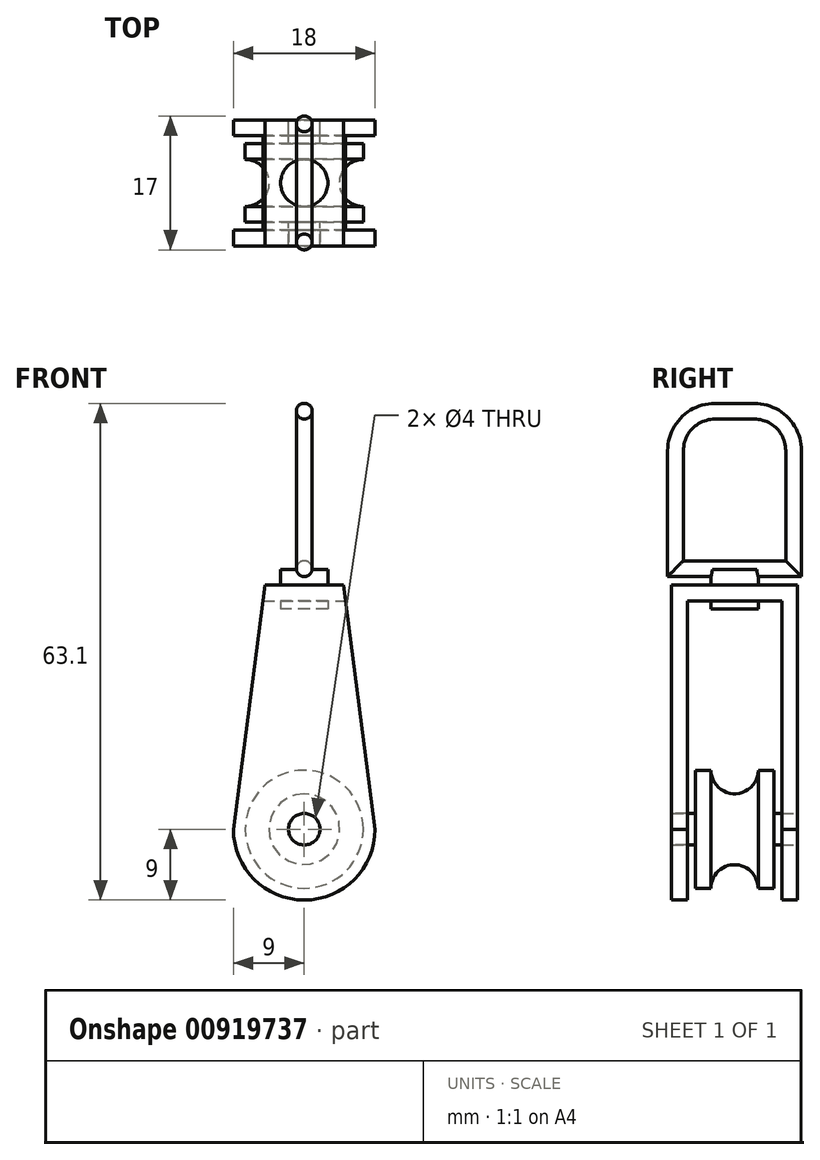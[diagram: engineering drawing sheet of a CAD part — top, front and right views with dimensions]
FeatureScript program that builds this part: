
annotation { "Feature Type Name" : "Feature", "Feature Type Description" : "" }
export const myFeature = defineFeature(function(context is Context, id is Id, definition is map)
    precondition{}
    {
        {
            var Q0;
            Q0=qCreatedBy(makeId("Right.planeOp"),FACE);
            var sketch = newSketch(context, id + "F0", { "sketchPlane" : qUnion([Q0])});
            skLineSegment(sketch, "E0", {"start": v(0, 0) * mm, "end": v(5, 0) * mm});
            skLineSegment(sketch, "E1", {"start": v(0, 0) * mm, "end": v(-5, 0) * mm});
            skLineSegment(sketch, "E2", {"start": v(0, 0) * mm, "end": v(0, 7.5) * mm, "construction": true});
            skPoint(sketch, "E3", {"position": v(0, 4.5) * mm});
            skLineSegment(sketch, "E4.0", {"start": v(3, 0) * mm, "end": v(3, 7.5) * mm, "construction": true});
            skLineSegment(sketch, "E5.0", {"start": v(-3, 0) * mm, "end": v(-3, 7.5) * mm, "construction": true});
            skArc(sketch, "E6", {"start": v(-3, 7.5) * mm, "mid": v(0, 4.5) * mm, "end": v(3, 7.5) * mm});
            skLineSegment(sketch, "E7", {"start": v(3, 7.5) * mm, "end": v(5, 7.5) * mm});
            skLineSegment(sketch, "E8", {"start": v(5, 7.5) * mm, "end": v(5, 0) * mm});
            skLineSegment(sketch, "E9", {"start": v(-3, 7.5) * mm, "end": v(-5, 7.5) * mm});
            skLineSegment(sketch, "E10", {"start": v(-5, 7.5) * mm, "end": v(-5, 0) * mm});
            skSolve(sketch);
        }
        {
            var Q0;
            Q0=makeQuery(id+"F0.imprint","IMPRINT",FACE,{"disambiguationData":[TD([[makeQuery(id+"F0.imprint","IMPRINT",EDGE,{"derivedFrom":sQuery(id+"F0.wireOp",EDGE,"E0")}),1.0]])]});
            var Q1;
            Q1=sQuery(id+"F0.wireOp",EDGE,"E1");
            revolve(context, id + "F1", {"surfaceOperationType" : NewSurfaceOperationType.NEW, "entities" : qUnion([Q0]), "axis" : qUnion([Q1]), "revolveType" : RevolveType.FULL});
        }
        {
            var Q0;
            Q0=makeQuery(id+"F1.opRevolve","SWEPT_FACE",FACE,{"disambiguationData":[OSD([sQuery(id+"F0.wireOp",EDGE,"E8")])]});
            var sketch = newSketch(context, id + "F2", { "sketchPlane" : qUnion([Q0])});
            skCircle(sketch, "E11", {"center": v(0, 0) * mm, "radius": 2 * mm});
            skSolve(sketch);
        }
        {
            var Q0;
            Q0=makeQuery(id+"F2.imprint","IMPRINT",FACE,{"disambiguationData":[TD([[makeQuery(id+"F2.imprint","IMPRINT",EDGE,{"derivedFrom":sQuery(id+"F2.wireOp",EDGE,"E11")}),1.0]])]});
            var Q1;
            Q1=makeQuery(id+"F1.opRevolve","SWEPT_FACE",FACE,{"disambiguationData":[OSD([sQuery(id+"F0.wireOp",EDGE,"E10")])]});
            extrude(context, id + "F3", {"entities" : qUnion([Q0]), "operationType" : NewBodyOperationType.ADD, "endBound" : BoundingType.UP_TO_SURFACE, "oppositeDirection" : true, "depth" : 25 * mm, "endBoundEntityFace" : qUnion([Q1]), "hasOffset" : true, "offsetDistance" : 3 * mm, "offsetOppositeDirection" : true, "hasSecondDirection" : true, "secondDirectionOppositeDirection" : false, "secondDirectionDepth" : 3 * mm});
        }
        {
            var Q0;
            Q0=makeQuery(id+"F3.opExtrude","CAP_FACE",FACE,{"disambiguationData":[OSD([sQuery(id+"F2.wireOp",EDGE,"E11")])],"isStart":true});
            var sketch = newSketch(context, id + "F4", { "sketchPlane" : qUnion([Q0])});
            skCircle(sketch, "E12.0", {"center": v(0, 0) * mm, "radius": 7.5 * mm});
            skCircle(sketch, "E13.0", {"center": v(0, 0) * mm, "radius": 2 * mm});
            skLineSegment(sketch, "E14", {"start": v(0, 0) * mm, "end": v(-7.5, 0) * mm, "construction": true});
            skLineSegment(sketch, "E15", {"start": v(0, 0) * mm, "end": v(7.5, 0) * mm, "construction": true});
            skLineSegment(sketch, "E16", {"start": v(7.5, 0) * mm, "end": v(9, 0) * mm, "construction": true});
            skLineSegment(sketch, "E17", {"start": v(-7.5, 0) * mm, "end": v(-9, 0) * mm, "construction": true});
            skLineSegment(sketch, "E18", {"start": v(0, 0) * mm, "end": v(0, -7.5) * mm, "construction": true});
            skLineSegment(sketch, "E19", {"start": v(0, -7.5) * mm, "end": v(0, -9) * mm, "construction": true});
            skArc(sketch, "E20", {"start": v(-9, 0) * mm, "mid": v(0, -9) * mm, "end": v(9, 0) * mm});
            skLineSegment(sketch, "E21", {"start": v(0, 0) * mm, "end": v(0, 49) * mm, "construction": true});
            skPoint(sketch, "E22", {"position": v(0, 33) * mm});
            skPoint(sketch, "E23", {"position": v(0, 31) * mm});
            skLineSegment(sketch, "E24", {"start": v(0, 31) * mm, "end": v(-5, 31) * mm});
            skLineSegment(sketch, "E25", {"start": v(0, 31) * mm, "end": v(5, 31) * mm});
            skLineSegment(sketch, "E26", {"start": v(5, 31) * mm, "end": v(9, 0) * mm});
            skLineSegment(sketch, "E27", {"start": v(-5, 31) * mm, "end": v(-9, 0) * mm});
            skSolve(sketch);
        }
        {
            var Q0;
            Q0=makeQuery(id+"F4.imprint","IMPRINT",FACE,{"disambiguationData":[TD([[makeQuery(id+"F4.imprint","IMPRINT",EDGE,{"derivedFrom":sQuery(id+"F4.wireOp",EDGE,"E12.0")}),-1.0]])]});
            var Q1;
            Q1=makeQuery(id+"F4.imprint","IMPRINT",FACE,{"disambiguationData":[TD([[makeQuery(id+"F4.imprint","IMPRINT",EDGE,{"derivedFrom":sQuery(id+"F4.wireOp",EDGE,"E12.0")}),1.0]])]});
            extrude(context, id + "F5", {"entities" : qUnion([Q0, Q1]), "oppositeDirection" : true, "depth" : 2 * mm, "offsetDistance" : 25 * mm});
        }
        {
            var Q0;
            Q0=makeQuery(id+"F5.opExtrude","SWEPT_BODY",BODY,{"disambiguationData":[OSD([sQuery(id+"F4.wireOp",EDGE,"E13.0"),sQuery(id+"F4.wireOp",EDGE,"E20"),sQuery(id+"F4.wireOp",EDGE,"E24"),sQuery(id+"F4.wireOp",EDGE,"E25"),sQuery(id+"F4.wireOp",EDGE,"E26"),sQuery(id+"F4.wireOp",EDGE,"E27")])]});
            var Q1;
            Q1=qCreatedBy(makeId("Front.planeOp"),FACE);
            mirror(context, id + "F6", {"entities" : qUnion([Q0]), "mirrorPlane" : qUnion([Q1])});
        }
        {
            var Q0;
            Q0=makeQuery(id+"F5.opExtrude","CAP_FACE",FACE,{"disambiguationData":[OSD([sQuery(id+"F4.wireOp",EDGE,"E13.0"),sQuery(id+"F4.wireOp",EDGE,"E20"),sQuery(id+"F4.wireOp",EDGE,"E24"),sQuery(id+"F4.wireOp",EDGE,"E25"),sQuery(id+"F4.wireOp",EDGE,"E26"),sQuery(id+"F4.wireOp",EDGE,"E27")])],"isStart":true});
            var sketch = newSketch(context, id + "F7", { "sketchPlane" : qUnion([Q0])});
            skLineSegment(sketch, "E28", {"start": v(0, 31) * mm, "end": v(0, 29) * mm, "construction": true});
            skLineSegment(sketch, "E29.0", {"start": v(-5, 31) * mm, "end": v(-9, 0) * mm});
            skLineSegment(sketch, "E30.0", {"start": v(5, 31) * mm, "end": v(9, 0) * mm});
            skLineSegment(sketch, "E31", {"start": v(0, 29) * mm, "end": v(-5.26, 29) * mm});
            skLineSegment(sketch, "E32", {"start": v(0, 29) * mm, "end": v(5.26, 29) * mm});
            skSolve(sketch);
        }
        {
            var Q0;
            {var subQ0=sQuery(id+"F7.wireOp",EDGE,"E31");Q0=makeQuery(id+"F7.imprint","IMPRINT",FACE,{"disambiguationData":[TD([[makeQuery(id+"F7.imprint","IMPRINT",EDGE,{"derivedFrom":subQ0}),-1.0]])]});}
            var Q1;
            Q1=makeQuery(id+"F6.opPattern","COPY",FACE,{"derivedFrom":makeQuery(id+"F5.opExtrude","CAP_FACE",FACE,{"disambiguationData":[OSD([sQuery(id+"F4.wireOp",EDGE,"E13.0"),sQuery(id+"F4.wireOp",EDGE,"E20"),sQuery(id+"F4.wireOp",EDGE,"E24"),sQuery(id+"F4.wireOp",EDGE,"E25"),sQuery(id+"F4.wireOp",EDGE,"E26"),sQuery(id+"F4.wireOp",EDGE,"E27")])],"isStart":false}),"instanceName":"1"});
            extrude(context, id + "F8", {"entities" : qUnion([Q0]), "operationType" : NewBodyOperationType.ADD, "endBound" : BoundingType.UP_TO_SURFACE, "oppositeDirection" : true, "depth" : 25 * mm, "endBoundEntityFace" : qUnion([Q1]), "offsetDistance" : 25 * mm});
        }
        {
            var Q0;
            {var subQ0=sQuery(id+"F4.wireOp",EDGE,"E25");var subQ1=sQuery(id+"F4.wireOp",EDGE,"E24");var subQ2=makeQuery(id+"F5.opExtrude","SWEPT_FACE",FACE,{"disambiguationData":[OSD([subQ1,subQ0])]});Q0=makeQuery(id+"F8.boolean.opBoolean","MERGE",FACE,{"derivedFrom":[subQ2,makeQuery(id+"F6.opPattern","COPY",FACE,{"derivedFrom":subQ2,"instanceName":"1"}),makeQuery(id+"F8.opExtrude","SWEPT_FACE",FACE,{"disambiguationData":[OSD([subQ1,subQ0])]})]});}
            var sketch = newSketch(context, id + "F9", { "sketchPlane" : qUnion([Q0])});
            skCircle(sketch, "E33", {"center": v(0, 0) * mm, "radius": 3 * mm});
            skSolve(sketch);
        }
        {
            var Q0;
            Q0=makeQuery(id+"F9.imprint","IMPRINT",FACE,{"disambiguationData":[TD([[makeQuery(id+"F9.imprint","IMPRINT",EDGE,{"derivedFrom":sQuery(id+"F9.wireOp",EDGE,"E33")}),1.0]])]});
            extrude(context, id + "F10", {"entities" : qUnion([Q0]), "operationType" : NewBodyOperationType.ADD, "depth" : 2 * mm, "offsetDistance" : 25 * mm, "hasSecondDirection" : true, "secondDirectionOppositeDirection" : true, "secondDirectionDepth" : 3 * mm});
        }
        {
            var Q0;
            Q0=qCreatedBy(makeId("Front.planeOp"),FACE);
            var sketch = newSketch(context, id + "F11", { "sketchPlane" : qUnion([Q0])});
            skLineSegment(sketch, "E34.0", {"start": v(-3, 33) * mm, "end": v(3, 33) * mm});
            skLineSegment(sketch, "E35", {"start": v(0, 33) * mm, "end": v(0, 33.1) * mm, "construction": true});
            skPoint(sketch, "E36", {"position": v(0, 33.1) * mm});
            skCircle(sketch, "E37", {"center": v(0, 33.1) * mm, "radius": 1 * mm});
            skSolve(sketch);
        }
        {
            var Q0;
            Q0=qCreatedBy(makeId("Right.planeOp"),FACE);
            var sketch = newSketch(context, id + "F12", { "sketchPlane" : qUnion([Q0])});
            skPoint(sketch, "E38.0", {"position": v(0, 33.1) * mm});
            skLineSegment(sketch, "E39", {"start": v(0, 33.1) * mm, "end": v(7.5, 33.1) * mm});
            skLineSegment(sketch, "E40", {"start": v(7.5, 33.1) * mm, "end": v(7.5, 48.1) * mm});
            skLineSegment(sketch, "E41", {"start": v(2.5, 53.1) * mm, "end": v(-2.5, 53.1) * mm});
            skLineSegment(sketch, "E42", {"start": v(-7.5, 48.1) * mm, "end": v(-7.5, 33.1) * mm});
            skLineSegment(sketch, "E43", {"start": v(-7.5, 33.1) * mm, "end": v(0, 33.1) * mm});
            skPoint(sketch, "E44.visualSharp", {"position": v(7.5, 53.1) * mm});
            skArc(sketch, "E44.filletArc", {"start": v(7.5, 48.1) * mm, "mid": v(6.04, 51.64) * mm, "end": v(2.5, 53.1) * mm});
            skPoint(sketch, "E45.visualSharp", {"position": v(-7.5, 53.1) * mm});
            skArc(sketch, "E45.filletArc", {"start": v(-2.5, 53.1) * mm, "mid": v(-6.04, 51.64) * mm, "end": v(-7.5, 48.1) * mm});
            skSolve(sketch);
        }
        {
            var Q0;
            Q0=makeQuery(id+"F11.imprint","IMPRINT",FACE,{"disambiguationData":[TD([[makeQuery(id+"F11.imprint","IMPRINT",EDGE,{"derivedFrom":sQuery(id+"F11.wireOp",EDGE,"E37")}),1.0]])]});
            var Q1;
            Q1=sQuery(id+"F12.wireOp",EDGE,"E39");
            var Q2;
            Q2=sQuery(id+"F12.wireOp",EDGE,"E40");
            var Q3;
            Q3=sQuery(id+"F12.wireOp",EDGE,"E44.filletArc");
            var Q4;
            Q4=sQuery(id+"F12.wireOp",EDGE,"E41");
            var Q5;
            Q5=sQuery(id+"F12.wireOp",EDGE,"E45.filletArc");
            var Q6;
            Q6=sQuery(id+"F12.wireOp",EDGE,"E42");
            var Q7;
            Q7=sQuery(id+"F12.wireOp",EDGE,"E43");
            sweep(context, id + "F13", {"operationType" : NewBodyOperationType.ADD, "profiles" : qUnion([Q0]), "path" : qUnion([Q1, Q2, Q3, Q4, Q5, Q6, Q7])});
        }
        {
            var Q0;
            Q0=qCreatedBy(makeId("Front.planeOp"),FACE);
            var sketch = newSketch(context, id + "F14", { "sketchPlane" : qUnion([Q0])});
            skLineSegment(sketch, "E46", {"start": v(0, 0) * mm, "end": v(0, 7.5) * mm, "construction": true});
            skLineSegment(sketch, "E47", {"start": v(3, 7.5) * mm, "end": v(5, 7.5) * mm});
            skLineSegment(sketch, "E48", {"start": v(-5, 7.5) * mm, "end": v(-3, 7.5) * mm});
            skLineSegment(sketch, "E49", {"start": v(-3, 7.5) * mm, "end": v(3, 7.5) * mm, "construction": true});
            skSolve(sketch);
        }
        {
            var Q0;
            Q0=qCreatedBy(makeId("Front.planeOp"),FACE);
            var sketch = newSketch(context, id + "F15", { "sketchPlane" : qUnion([Q0])});
            skLineSegment(sketch, "E50.0", {"start": v(-1, 48.1) * mm, "end": v(1, 48.1) * mm});
            skLineSegment(sketch, "E51", {"start": v(0, 48.1) * mm, "end": v(0, 50.6) * mm});
            skLineSegment(sketch, "E52", {"start": v(0, 50.6) * mm, "end": v(1.1, 50.6) * mm});
            skSolve(sketch);
        }
    });
